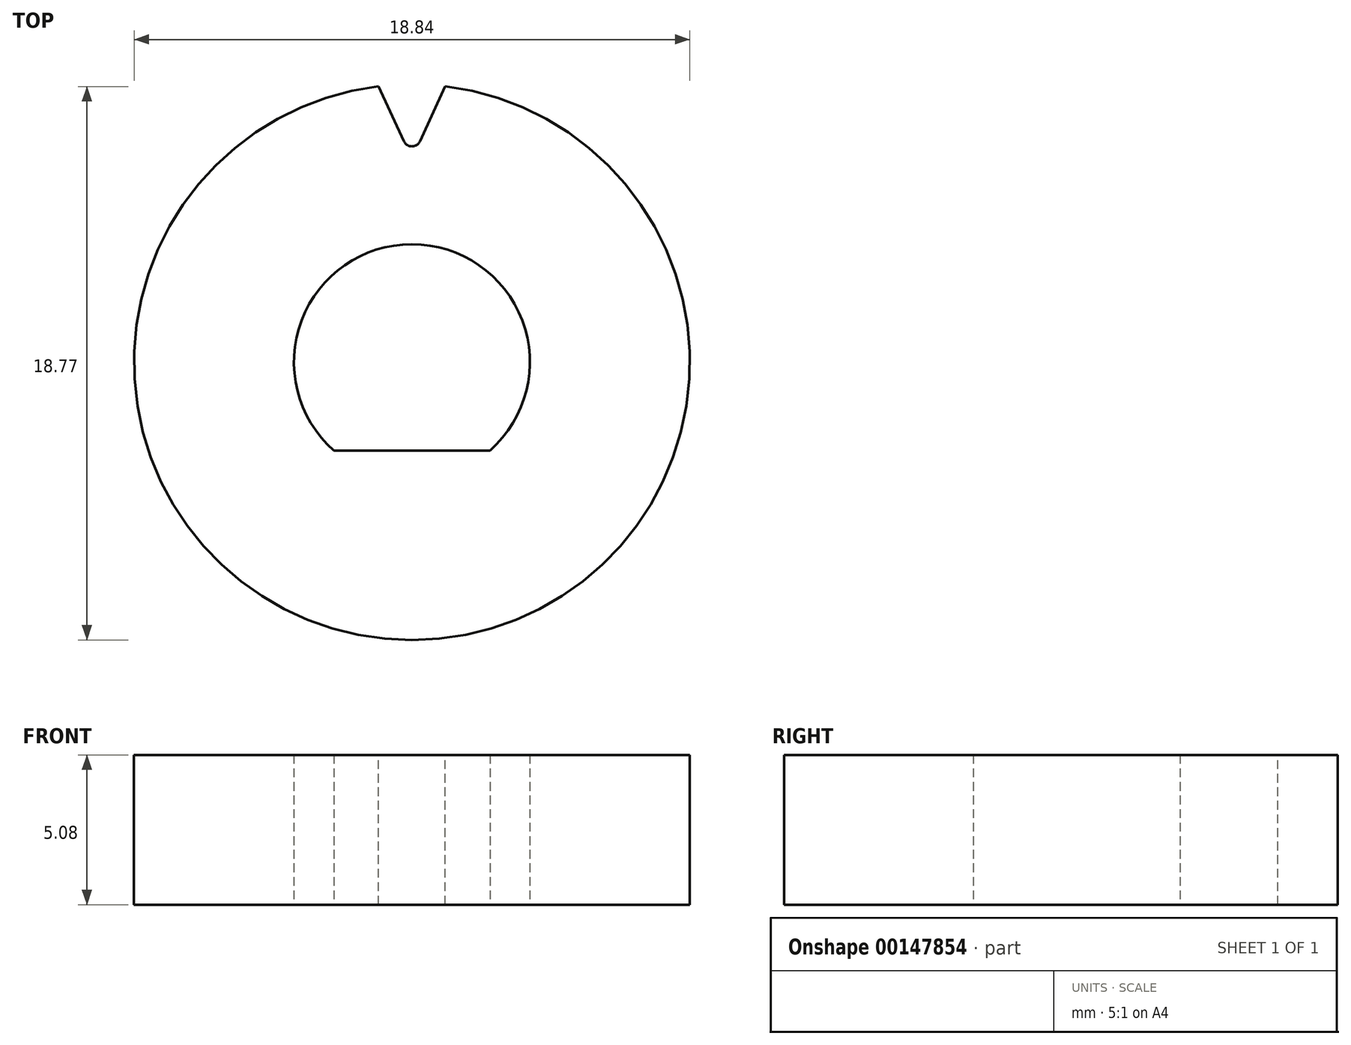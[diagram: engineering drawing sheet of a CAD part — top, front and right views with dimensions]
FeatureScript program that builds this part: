
annotation { "Feature Type Name" : "Feature", "Feature Type Description" : "" }
export const myFeature = defineFeature(function(context is Context, id is Id, definition is map)
    precondition{}
    {
        {
            var Q0;
            Q0=qCreatedBy(makeId("Top.planeOp"),FACE);
            var sketch = newSketch(context, id + "F0", { "sketchPlane" : qUnion([Q0])});
            skArc(sketch, "E0", {"start": v(2.65, -3) * mm, "mid": v(0, 4) * mm, "end": v(-2.65, -3) * mm});
            skCircle(sketch, "E1", {"center": v(0, 0) * mm, "radius": 9.42 * mm});
            skLineSegment(sketch, "E2", {"start": v(0, 0) * mm, "end": v(0, -3) * mm, "construction": true});
            skLineSegment(sketch, "E3", {"start": v(-2.65, -3) * mm, "end": v(2.65, -3) * mm});
            skSolve(sketch);
        }
        {
            var Q0;
            Q0=makeQuery(id+"F0.imprint","IMPRINT",FACE,{"disambiguationData":[TD([[makeQuery(id+"F0.imprint","IMPRINT",EDGE,{"derivedFrom":sQuery(id+"F0.wireOp",EDGE,"d7zeTPih-CRss-xDOh-gPdP-rmPCdwzH7cdN.left")}),1.0]])]});
            var Q1;
            Q1=makeQuery(id+"F0.imprint","IMPRINT",FACE,{"disambiguationData":[TD([[makeQuery(id+"F0.imprint","IMPRINT",EDGE,{"derivedFrom":sQuery(id+"F0.wireOp",EDGE,"E0")}),-1.0]])]});
            extrude(context, id + "F1", {"entities" : qUnion([Q0, Q1]), "depth" : 5.08 * mm});
        }
        {
            var Q0;
            Q0=makeQuery(id+"F1.opExtrude","CAP_FACE",FACE,{"disambiguationData":[OSD([sQuery(id+"F0.wireOp",EDGE,"d7zeTPih-CRss-xDOh-gPdP-rmPCdwzH7cdN.left"),sQuery(id+"F0.wireOp",EDGE,"d7zeTPih-CRss-xDOh-gPdP-rmPCdwzH7cdN.right"),sQuery(id+"F0.wireOp",EDGE,"E0"),sQuery(id+"F0.wireOp",EDGE,"xnxmVwjl-FvSF-m7sj-be2U-u85gZZGoORGZ"),sQuery(id+"F0.wireOp",EDGE,"E1")])],"isStart":false});
            var sketch = newSketch(context, id + "F2", { "sketchPlane" : qUnion([Q0])});
            skLineSegment(sketch, "E4", {"start": v(0, 0) * mm, "end": v(0, 9.42) * mm, "construction": true});
            skLineSegment(sketch, "E5", {"start": v(0, 0) * mm, "end": v(0.78, 9.39) * mm, "construction": true});
            skArc(sketch, "E6", {"start": v(1.13, 9.35) * mm, "mid": v(0, 9.42) * mm, "end": v(-1.13, 9.35) * mm});
            skLineSegment(sketch, "E7", {"start": v(-1.13, 9.35) * mm, "end": v(-0.27, 7.5) * mm});
            skLineSegment(sketch, "E8", {"start": v(1.13, 9.35) * mm, "end": v(0.27, 7.5) * mm});
            skPoint(sketch, "E9", {"position": v(0.7, 8.42) * mm});
            skArc(sketch, "E10", {"start": v(-0.27, 7.5) * mm, "mid": v(0, 7.32) * mm, "end": v(0.27, 7.5) * mm});
            skSolve(sketch);
        }
        {
            var Q0;
            Q0=qSketchRegion(id+"F2",true);
            var Q1;
            Q1=makeQuery(id+"F1.opExtrude","CAP_FACE",FACE,{"disambiguationData":[OSD([sQuery(id+"F0.wireOp",EDGE,"d7zeTPih-CRss-xDOh-gPdP-rmPCdwzH7cdN.left"),sQuery(id+"F0.wireOp",EDGE,"d7zeTPih-CRss-xDOh-gPdP-rmPCdwzH7cdN.right"),sQuery(id+"F0.wireOp",EDGE,"E0"),sQuery(id+"F0.wireOp",EDGE,"xnxmVwjl-FvSF-m7sj-be2U-u85gZZGoORGZ"),sQuery(id+"F0.wireOp",EDGE,"E1")])],"isStart":true});
            extrude(context, id + "F3", {"entities" : qUnion([Q0]), "operationType" : NewBodyOperationType.REMOVE, "endBound" : BoundingType.UP_TO_SURFACE, "oppositeDirection" : true, "endBoundEntityFace" : qUnion([Q1]), "depth" : 25.4 * mm});
        }
    });
